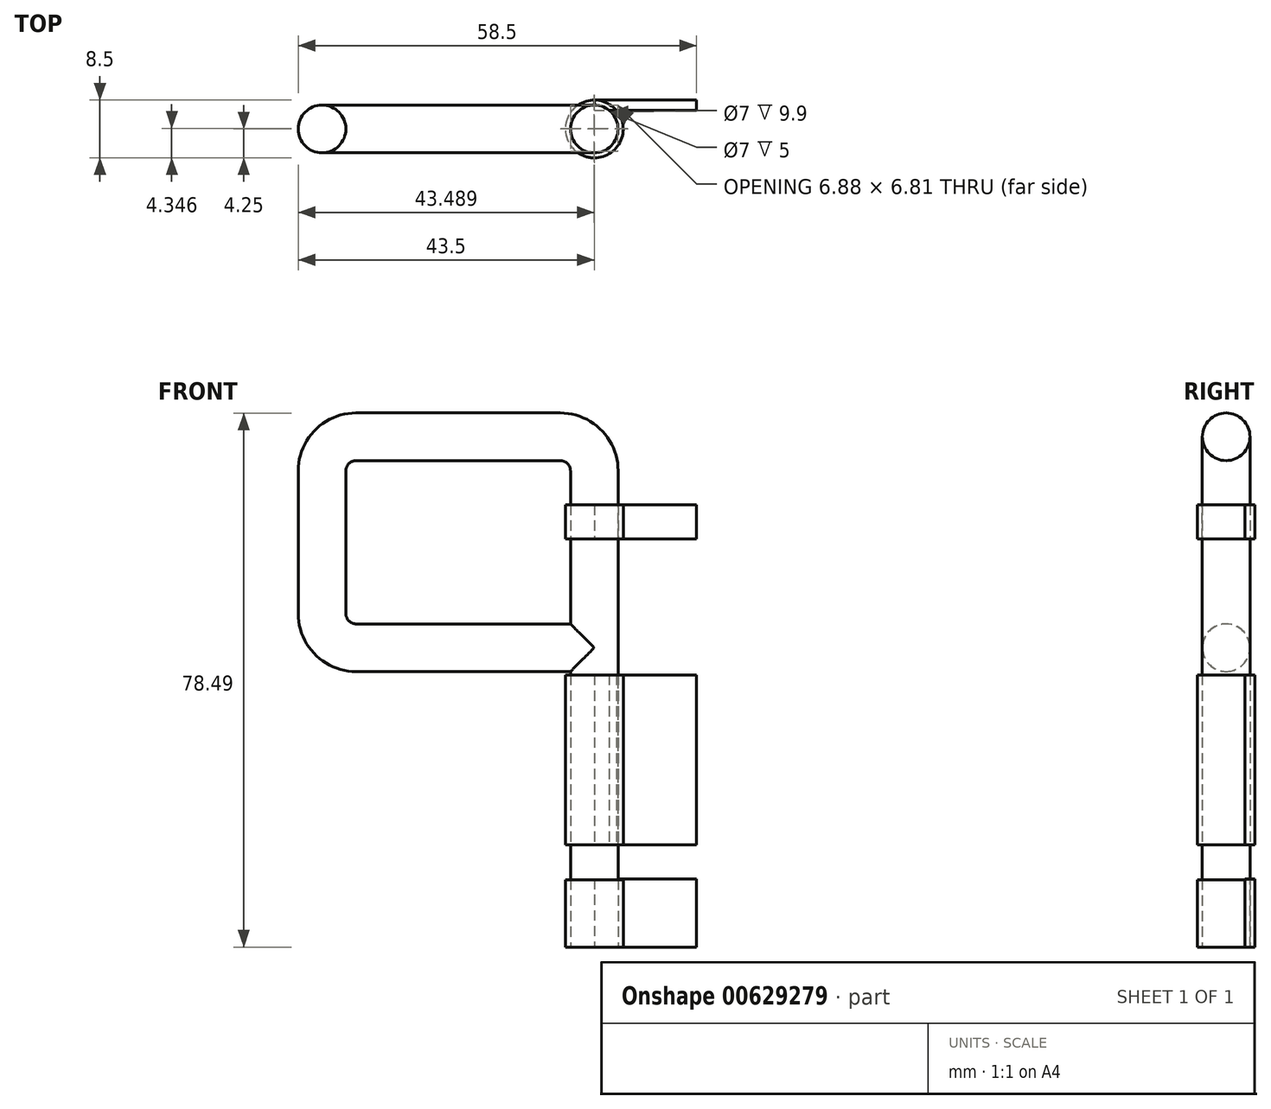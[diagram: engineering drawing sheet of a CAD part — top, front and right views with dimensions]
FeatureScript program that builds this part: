
annotation { "Feature Type Name" : "Feature", "Feature Type Description" : "" }
export const myFeature = defineFeature(function(context is Context, id is Id, definition is map)
    precondition{}
    {
        {
            var Q0;
            Q0=qCreatedBy(makeId("Front.planeOp"),FACE);
            var sketch = newSketch(context, id + "F0", { "sketchPlane" : qUnion([Q0])});
            skLineSegment(sketch, "E0.bottom", {"start": v(0, 10) * mm, "end": v(15, 10) * mm});
            skLineSegment(sketch, "E0.top", {"start": v(0, 0) * mm, "end": v(15, 0) * mm});
            skLineSegment(sketch, "E0.left", {"start": v(0, 10) * mm, "end": v(0, 0) * mm});
            skLineSegment(sketch, "E0.right", {"start": v(15, 10) * mm, "end": v(15, 0) * mm});
            skLineSegment(sketch, "E1", {"start": v(0, 0) * mm, "end": v(0, 60) * mm});
            skLineSegment(sketch, "E2.bottom", {"start": v(0, 65) * mm, "end": v(15, 65) * mm});
            skLineSegment(sketch, "E2.top", {"start": v(0, 60) * mm, "end": v(15, 60) * mm});
            skLineSegment(sketch, "E2.left", {"start": v(0, 65) * mm, "end": v(0, 60) * mm});
            skLineSegment(sketch, "E2.right", {"start": v(15, 65) * mm, "end": v(15, 60) * mm});
            skPoint(sketch, "E3", {"position": v(0, 60) * mm});
            skLineSegment(sketch, "E4.bottom", {"start": v(0, 40) * mm, "end": v(15, 40) * mm});
            skLineSegment(sketch, "E4.top", {"start": v(0, 15) * mm, "end": v(15, 15) * mm});
            skLineSegment(sketch, "E4.left", {"start": v(0, 40) * mm, "end": v(0, 15) * mm});
            skLineSegment(sketch, "E4.right", {"start": v(15, 40) * mm, "end": v(15, 15) * mm});
            skLineSegment(sketch, "E5.bottom", {"start": v(8, 60) * mm, "end": v(15, 60) * mm});
            skLineSegment(sketch, "E5.top", {"start": v(8, 40) * mm, "end": v(15, 40) * mm});
            skLineSegment(sketch, "E5.left", {"start": v(8, 60) * mm, "end": v(8, 40) * mm});
            skLineSegment(sketch, "E5.right", {"start": v(15, 60) * mm, "end": v(15, 40) * mm});
            skSolve(sketch);
        }
        {
            var Q0;
            Q0=qCreatedBy(makeId("Top.planeOp"),FACE);
            var sketch = newSketch(context, id + "F1", { "sketchPlane" : qUnion([Q0])});
            skCircle(sketch, "E6", {"center": v(0, -4.25) * mm, "radius": 4.25 * mm});
            skCircle(sketch, "E7", {"center": v(0, -4.25) * mm, "radius": 3.5 * mm});
            skSolve(sketch);
        }
        {
            var Q0;
            {var subQ0=sQuery(id+"F0.wireOp",EDGE,"E0.bottom");Q0=makeQuery(id+"F0.imprint","IMPRINT",FACE,{"disambiguationData":[TD([[makeQuery(id+"F0.imprint","IMPRINT",EDGE,{"derivedFrom":subQ0}),-1.0]])]});}
            var Q1;
            Q1=makeQuery(id+"F0.imprint","IMPRINT",FACE,{"disambiguationData":[TD([[makeQuery(id+"F0.imprint","IMPRINT",EDGE,{"derivedFrom":sQuery(id+"F0.wireOp",EDGE,"E4.bottom")}),-1.0]])]});
            var Q2;
            Q2=makeQuery(id+"F0.imprint","IMPRINT",FACE,{"disambiguationData":[TD([[makeQuery(id+"F0.imprint","IMPRINT",EDGE,{"derivedFrom":sQuery(id+"F0.wireOp",EDGE,"E2.bottom")}),-1.0]])]});
            var Q3;
            Q3=makeQuery(id+"F0.imprint","IMPRINT",FACE,{"disambiguationData":[TD([[makeQuery(id+"F0.imprint","IMPRINT",EDGE,{"derivedFrom":sQuery(id+"F0.wireOp",EDGE,"E5.bottom")}),-1.0]])]});
            extrude(context, id + "F2", {"entities" : qUnion([Q0, Q1, Q2, Q3]), "depth" : 1.5 * mm, "offsetDistance" : 25 * mm});
        }
        {
            var Q0;
            Q0=makeQuery(id+"F1.imprint","IMPRINT",FACE,{"disambiguationData":[TD([[makeQuery(id+"F1.imprint","IMPRINT",EDGE,{"derivedFrom":sQuery(id+"F1.wireOp",EDGE,"E6")}),1.0]])]});
            extrude(context, id + "F3", {"entities" : qUnion([Q0]), "depth" : 9.9 * mm, "offsetDistance" : 25 * mm});
        }
        {
            var Q0;
            Q0=sQuery(id+"F0.wireOp",EDGE,"E4.top");
            cPlane(context, id + "F4", {"entities" : qUnion([Q0]), "cplaneType" : CPlaneType.LINE_ANGLE, "offset" : 25 * mm, "angle" : 90 * degree, "width" : 150 * mm, "height" : 150 * mm});
        }
        {
            var Q0;
            Q0=qCreatedBy(id+"F4.planeOp",FACE);
            var sketch = newSketch(context, id + "F5", { "sketchPlane" : qUnion([Q0])});
            skCircle(sketch, "E8", {"center": v(0, -4.25) * mm, "radius": 4.25 * mm});
            skCircle(sketch, "E9", {"center": v(0, -4.25) * mm, "radius": 3.5 * mm});
            skSolve(sketch);
        }
        {
            var Q0;
            Q0=sQuery(id+"F0.wireOp",EDGE,"E2.top");
            cPlane(context, id + "F6", {"entities" : qUnion([Q0]), "cplaneType" : CPlaneType.LINE_ANGLE, "offset" : 25 * mm, "angle" : 90 * degree, "width" : 150 * mm, "height" : 150 * mm});
        }
        {
            var Q0;
            Q0=qCreatedBy(id+"F6.planeOp",FACE);
            var sketch = newSketch(context, id + "F7", { "sketchPlane" : qUnion([Q0])});
            skCircle(sketch, "E10", {"center": v(0, -4.25) * mm, "radius": 4.25 * mm});
            skCircle(sketch, "E11", {"center": v(0, -4.25) * mm, "radius": 3.5 * mm});
            skSolve(sketch);
        }
        {
            var Q0;
            Q0=makeQuery(id+"F7.imprint","IMPRINT",FACE,{"disambiguationData":[TD([[makeQuery(id+"F7.imprint","IMPRINT",EDGE,{"derivedFrom":sQuery(id+"F7.wireOp",EDGE,"E10")}),1.0]])]});
            extrude(context, id + "F8", {"entities" : qUnion([Q0]), "depth" : 5 * mm, "offsetDistance" : 25 * mm});
        }
        {
            var Q0;
            Q0=makeQuery(id+"F5.imprint","IMPRINT",FACE,{"disambiguationData":[TD([[makeQuery(id+"F5.imprint","IMPRINT",EDGE,{"derivedFrom":sQuery(id+"F5.wireOp",EDGE,"E8")}),1.0]])]});
            extrude(context, id + "F9", {"entities" : qUnion([Q0]), "operationType" : NewBodyOperationType.ADD, "depth" : 25 * mm, "offsetDistance" : 25 * mm});
        }
        {
            var Q0;
            Q0=sQuery(id+"F5.wireOp",VERTEX,"E8.center");
            var Q1;
            Q1=qCreatedBy(makeId("Front.planeOp"),FACE);
            cPlane(context, id + "F10", {"entities" : qUnion([Q0, Q1]), "cplaneType" : CPlaneType.PLANE_POINT, "offset" : 25 * mm, "width" : 150 * mm, "height" : 150 * mm});
        }
        {
            var Q0;
            Q0=qCreatedBy(id+"F10.planeOp",FACE);
            var sketch = newSketch(context, id + "F11", { "sketchPlane" : qUnion([Q0])});
            skLineSegment(sketch, "E12", {"start": v(0, 0) * mm, "end": v(0, 70) * mm});
            skLineSegment(sketch, "E13", {"start": v(-5, 75) * mm, "end": v(-35, 75) * mm});
            skLineSegment(sketch, "E14", {"start": v(-40, 70) * mm, "end": v(-40, 49) * mm});
            skLineSegment(sketch, "E15", {"start": v(-35, 44) * mm, "end": v(-0.1, 44) * mm});
            skPoint(sketch, "E16.visualSharp", {"position": v(-40, 44) * mm});
            skArc(sketch, "E16.filletArc", {"start": v(-40, 49) * mm, "mid": v(-38.54, 45.46) * mm, "end": v(-35, 44) * mm});
            skPoint(sketch, "E17.visualSharp", {"position": v(-40, 75) * mm});
            skArc(sketch, "E17.filletArc", {"start": v(-35, 75) * mm, "mid": v(-38.54, 73.53) * mm, "end": v(-40, 70) * mm});
            skPoint(sketch, "E18.visualSharp", {"position": v(0, 75) * mm});
            skArc(sketch, "E18.filletArc", {"start": v(0, 70) * mm, "mid": v(-1.46, 73.53) * mm, "end": v(-5, 75) * mm});
            skPoint(sketch, "E19", {"position": v(0, 44) * mm});
            skLineSegment(sketch, "E20", {"start": v(0, 44) * mm, "end": v(-0.06, 44) * mm});
            skSolve(sketch);
        }
        {
            var Q0;
            Q0=makeQuery(id+"F1.imprint","IMPRINT",FACE,{"disambiguationData":[TD([[makeQuery(id+"F1.imprint","IMPRINT",EDGE,{"derivedFrom":sQuery(id+"F1.wireOp",EDGE,"E7")}),1.0]])]});
            var Q1;
            Q1=sQuery(id+"F11.wireOp",EDGE,"E12");
            var Q2;
            Q2=sQuery(id+"F11.wireOp",EDGE,"E18.filletArc");
            var Q3;
            Q3=sQuery(id+"F11.wireOp",EDGE,"E13");
            var Q4;
            Q4=sQuery(id+"F11.wireOp",EDGE,"E17.filletArc");
            var Q5;
            Q5=sQuery(id+"F11.wireOp",EDGE,"E14");
            var Q6;
            Q6=sQuery(id+"F11.wireOp",EDGE,"E16.filletArc");
            var Q7;
            Q7=sQuery(id+"F11.wireOp",EDGE,"E15");
            sweep(context, id + "F12", {"profiles" : qUnion([Q0]), "path" : qUnion([Q1, Q2, Q3, Q4, Q5, Q6, Q7])});
        }
    });
